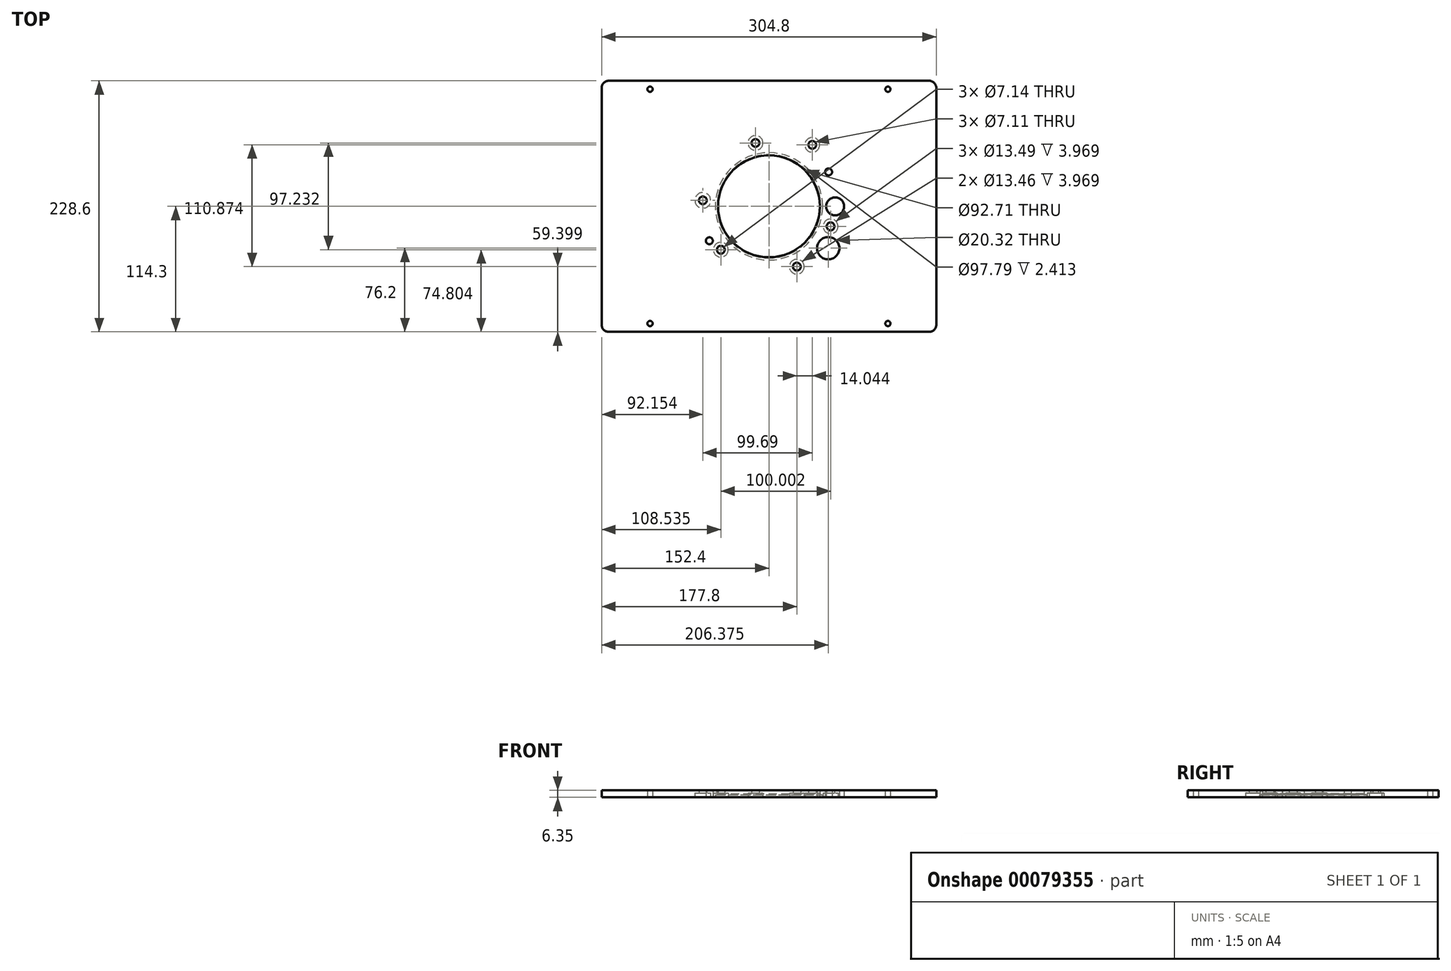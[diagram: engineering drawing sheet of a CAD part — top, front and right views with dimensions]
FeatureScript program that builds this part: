
annotation { "Feature Type Name" : "Feature", "Feature Type Description" : "" }
export const myFeature = defineFeature(function(context is Context, id is Id, definition is map)
    precondition{}
    {
        {
            var Q0;
            Q0=qCreatedBy(makeId("Top.planeOp"),FACE);
            var sketch = newSketch(context, id + "F0", { "sketchPlane" : qUnion([Q0])});
            skLineSegment(sketch, "E0.bottom", {"start": v(146.05, 114.3) * mm, "end": v(-146.05, 114.3) * mm});
            skLineSegment(sketch, "E0.top", {"start": v(146.05, -114.3) * mm, "end": v(-146.05, -114.3) * mm});
            skLineSegment(sketch, "E0.left", {"start": v(152.4, 107.95) * mm, "end": v(152.4, -107.95) * mm});
            skLineSegment(sketch, "E0.right", {"start": v(-152.4, 107.95) * mm, "end": v(-152.4, -107.95) * mm});
            skPoint(sketch, "E0.middle", {"position": v(0, 0) * mm});
            skPoint(sketch, "E1.visualSharp", {"position": v(-152.4, 114.3) * mm});
            skArc(sketch, "E1.filletArc", {"start": v(-146.05, 114.3) * mm, "mid": v(-150.54, 112.44) * mm, "end": v(-152.4, 107.95) * mm});
            skPoint(sketch, "E2.visualSharp", {"position": v(-152.4, -114.3) * mm});
            skArc(sketch, "E2.filletArc", {"start": v(-152.4, -107.95) * mm, "mid": v(-150.54, -112.44) * mm, "end": v(-146.05, -114.3) * mm});
            skPoint(sketch, "E3.visualSharp", {"position": v(152.4, -114.3) * mm});
            skArc(sketch, "E3.filletArc", {"start": v(146.05, -114.3) * mm, "mid": v(150.54, -112.44) * mm, "end": v(152.4, -107.95) * mm});
            skPoint(sketch, "E4.visualSharp", {"position": v(152.4, 114.3) * mm});
            skArc(sketch, "E4.filletArc", {"start": v(152.4, 107.95) * mm, "mid": v(150.54, 112.44) * mm, "end": v(146.05, 114.3) * mm});
            skSolve(sketch);
        }
        {
            var Q0;
            Q0 = qSketchRegion(id + "F0", true);
            var Q1;
            Q1=sQuery(id+"F0.wireOp",EDGE,"E0.left");
            extrude(context, id + "F1", {"entities" : qUnion([Q0]), "surfaceEntities" : qUnion([Q1]), "depth" : 6.35 * mm});
        }
        {
            var Q0;
            Q0=makeQuery(id+"F1.opExtrude","CAP_FACE",FACE,{"disambiguationData":[OSD([sQuery(id+"F0.wireOp",EDGE,"E0.bottom"),sQuery(id+"F0.wireOp",EDGE,"E0.top"),sQuery(id+"F0.wireOp",EDGE,"E0.left"),sQuery(id+"F0.wireOp",EDGE,"E0.right"),sQuery(id+"F0.wireOp",EDGE,"E1.filletArc"),sQuery(id+"F0.wireOp",EDGE,"E2.filletArc"),sQuery(id+"F0.wireOp",EDGE,"E3.filletArc"),sQuery(id+"F0.wireOp",EDGE,"E4.filletArc")])],"isStart":true});
            var sketch = newSketch(context, id + "F2", { "sketchPlane" : qUnion([Q0])});
            skCircle(sketch, "E5", {"center": v(0, 0) * mm, "radius": 46.35 * mm});
            skCircle(sketch, "E6", {"center": v(60.32, 0) * mm, "radius": 8.18 * mm});
            skCircle(sketch, "E7", {"center": v(53.97, 38.1) * mm, "radius": 10.16 * mm});
            skCircle(sketch, "E8", {"center": v(54.3, -31.35) * mm, "radius": 3.18 * mm});
            skCircle(sketch, "E9", {"center": v(-54.3, 31.35) * mm, "radius": 3.18 * mm});
            skLineSegment(sketch, "E10", {"start": v(54.3, -31.35) * mm, "end": v(-54.3, 31.35) * mm, "construction": true});
            skLineSegment(sketch, "E11", {"start": v(23.18, 40.14) * mm, "end": v(-23.18, -40.14) * mm, "construction": true});
            skCircle(sketch, "E12", {"center": v(0, 0) * mm, "radius": 60.5 * mm, "construction": true});
            skCircle(sketch, "E13", {"center": v(25.4, 54.9) * mm, "radius": 3.56 * mm});
            skCircle(sketch, "E14", {"center": v(-60.25, -5.45) * mm, "radius": 3.56 * mm});
            skLineSegment(sketch, "E15", {"start": v(25.4, 54.9) * mm, "end": v(0, 0) * mm, "construction": true});
            skLineSegment(sketch, "E16", {"start": v(-60.25, -5.45) * mm, "end": v(0, 0) * mm, "construction": true});
            skLineSegment(sketch, "E17", {"start": v(0, 0) * mm, "end": v(39.44, -55.97) * mm, "construction": true});
            skCircle(sketch, "E18", {"center": v(39.44, -55.97) * mm, "radius": 3.56 * mm});
            skCircle(sketch, "E19", {"center": v(108.33, 106.68) * mm, "radius": 2.38 * mm});
            skCircle(sketch, "E20", {"center": v(-108.33, 106.68) * mm, "radius": 2.38 * mm});
            skCircle(sketch, "E21", {"center": v(-108.33, -106.68) * mm, "radius": 2.38 * mm});
            skCircle(sketch, "E22", {"center": v(108.33, -106.68) * mm, "radius": 2.38 * mm});
            skSolve(sketch);
        }
        {
            var Q0;
            Q0 = qSketchRegion(id + "F2", true);
            extrude(context, id + "F3", {"entities" : qUnion([Q0]), "operationType" : NewBodyOperationType.REMOVE, "endBound" : BoundingType.THROUGH_ALL, "oppositeDirection" : true, "depth" : 25.4 * mm});
        }
        {
            var Q0;
            Q0=makeQuery(id+"F1.opExtrude","CAP_FACE",FACE,{"disambiguationData":[OSD([sQuery(id+"F0.wireOp",EDGE,"E0.bottom"),sQuery(id+"F0.wireOp",EDGE,"E0.top"),sQuery(id+"F0.wireOp",EDGE,"E0.left"),sQuery(id+"F0.wireOp",EDGE,"E0.right"),sQuery(id+"F0.wireOp",EDGE,"E1.filletArc"),sQuery(id+"F0.wireOp",EDGE,"E2.filletArc"),sQuery(id+"F0.wireOp",EDGE,"E3.filletArc"),sQuery(id+"F0.wireOp",EDGE,"E4.filletArc")])],"isStart":true});
            var sketch = newSketch(context, id + "F4", { "sketchPlane" : qUnion([Q0])});
            skCircle(sketch, "E23", {"center": v(0, 0) * mm, "radius": 48.9 * mm});
            skSolve(sketch);
        }
        {
            var Q0;
            Q0 = qSketchRegion(id + "F4", true);
            extrude(context, id + "F5", {"entities" : qUnion([Q0]), "operationType" : NewBodyOperationType.REMOVE, "oppositeDirection" : true, "depth" : 2.41 * mm});
        }
        {
            var Q0;
            Q0=makeQuery(id+"F5.boolean.opBoolean","INTERSECT",EDGE,{"derivedFrom":[makeQuery(id+"F3.boolean.opBoolean","COPY",FACE,{"derivedFrom":makeQuery(id+"F3.opExtrude","SWEPT_FACE",FACE,{"disambiguationData":[OSD([sQuery(id+"F2.wireOp",EDGE,"E5")])]})}),makeQuery(id+"F5.opExtrude","CAP_FACE",FACE,{"disambiguationData":[OSD([sQuery(id+"F4.wireOp",EDGE,"E23")])],"isStart":false})]});
            chamfer(context, id + "F6", {"entities" : qUnion([Q0]), "width" : 0.8 * mm, "tangentPropagation" : true});
        }
        {
            var Q0;
            Q0=makeQuery(id+"F1.opExtrude","CAP_FACE",FACE,{"disambiguationData":[OSD([sQuery(id+"F0.wireOp",EDGE,"E0.bottom"),sQuery(id+"F0.wireOp",EDGE,"E0.top"),sQuery(id+"F0.wireOp",EDGE,"E0.left"),sQuery(id+"F0.wireOp",EDGE,"E0.right"),sQuery(id+"F0.wireOp",EDGE,"E1.filletArc"),sQuery(id+"F0.wireOp",EDGE,"E2.filletArc"),sQuery(id+"F0.wireOp",EDGE,"E3.filletArc"),sQuery(id+"F0.wireOp",EDGE,"E4.filletArc")])],"isStart":true});
            var sketch = newSketch(context, id + "F7", { "sketchPlane" : qUnion([Q0])});
            skCircle(sketch, "E24", {"center": v(39.44, -55.97) * mm, "radius": 6.73 * mm});
            skCircle(sketch, "E25", {"center": v(-60.25, -5.45) * mm, "radius": 7.15 * mm});
            skCircle(sketch, "E26", {"center": v(25.4, 54.9) * mm, "radius": 6.73 * mm});
            skSolve(sketch);
        }
        {
            var Q0;
            Q0 = qSketchRegion(id + "F7", true);
            extrude(context, id + "F8", {"entities" : qUnion([Q0]), "operationType" : NewBodyOperationType.REMOVE, "oppositeDirection" : true, "depth" : 3.97 * mm});
        }
        {
            var Q0;
            Q0=makeQuery(id+"F1.opExtrude","CAP_FACE",FACE,{"disambiguationData":[OSD([sQuery(id+"F0.wireOp",EDGE,"E0.bottom"),sQuery(id+"F0.wireOp",EDGE,"E0.top"),sQuery(id+"F0.wireOp",EDGE,"E0.left"),sQuery(id+"F0.wireOp",EDGE,"E0.right"),sQuery(id+"F0.wireOp",EDGE,"E1.filletArc"),sQuery(id+"F0.wireOp",EDGE,"E2.filletArc"),sQuery(id+"F0.wireOp",EDGE,"E3.filletArc"),sQuery(id+"F0.wireOp",EDGE,"E4.filletArc")])],"isStart":true});
            var sketch = newSketch(context, id + "F9", { "sketchPlane" : qUnion([Q0])});
            skCircle(sketch, "E27", {"center": v(0, 0) * mm, "radius": 59.03 * mm, "construction": true});
            skCircle(sketch, "E28", {"center": v(56.14, 18.24) * mm, "radius": 3.57 * mm});
            skCircle(sketch, "E29", {"center": v(-12.27, -57.74) * mm, "radius": 3.57 * mm});
            skCircle(sketch, "E30", {"center": v(-43.86, 39.5) * mm, "radius": 3.57 * mm});
            skLineSegment(sketch, "E31", {"start": v(-12.27, -57.74) * mm, "end": v(0, 0) * mm, "construction": true});
            skLineSegment(sketch, "E32", {"start": v(-43.86, 39.5) * mm, "end": v(0, 0) * mm, "construction": true});
            skLineSegment(sketch, "E33", {"start": v(0, 0) * mm, "end": v(56.14, 18.24) * mm, "construction": true});
            skLineSegment(sketch, "E34", {"start": v(0, 0) * mm, "end": v(-152.4, 0) * mm, "construction": true});
            skLineSegment(sketch, "E35", {"start": v(0, 0) * mm, "end": v(0, -114.3) * mm, "construction": true});
            skLineSegment(sketch, "E36", {"start": v(0, 0) * mm, "end": v(0, 114.3) * mm, "construction": true});
            skLineSegment(sketch, "E37", {"start": v(-47.36, 40.24) * mm, "end": v(59.63, 17.5) * mm, "construction": true});
            skSolve(sketch);
        }
        {
            var Q0;
            Q0 = qSketchRegion(id + "F9", true);
            extrude(context, id + "F10", {"entities" : qUnion([Q0]), "operationType" : NewBodyOperationType.REMOVE, "endBound" : BoundingType.THROUGH_ALL, "oppositeDirection" : true, "depth" : 25.4 * mm});
        }
        {
            var Q0;
            Q0=makeQuery(id+"F1.opExtrude","CAP_FACE",FACE,{"disambiguationData":[OSD([sQuery(id+"F0.wireOp",EDGE,"E0.bottom"),sQuery(id+"F0.wireOp",EDGE,"E0.top"),sQuery(id+"F0.wireOp",EDGE,"E0.left"),sQuery(id+"F0.wireOp",EDGE,"E0.right"),sQuery(id+"F0.wireOp",EDGE,"E1.filletArc"),sQuery(id+"F0.wireOp",EDGE,"E2.filletArc"),sQuery(id+"F0.wireOp",EDGE,"E3.filletArc"),sQuery(id+"F0.wireOp",EDGE,"E4.filletArc")])],"isStart":true});
            var sketch = newSketch(context, id + "F11", { "sketchPlane" : qUnion([Q0])});
            skCircle(sketch, "E38", {"center": v(-12.27, -57.74) * mm, "radius": 6.75 * mm});
            skCircle(sketch, "E39", {"center": v(56.14, 18.24) * mm, "radius": 6.75 * mm});
            skCircle(sketch, "E40", {"center": v(-43.86, 39.5) * mm, "radius": 6.75 * mm});
            skSolve(sketch);
        }
        {
            var Q0;
            Q0 = qSketchRegion(id + "F11", true);
            extrude(context, id + "F12", {"entities" : qUnion([Q0]), "operationType" : NewBodyOperationType.REMOVE, "oppositeDirection" : true, "depth" : 3.97 * mm});
        }
    });
